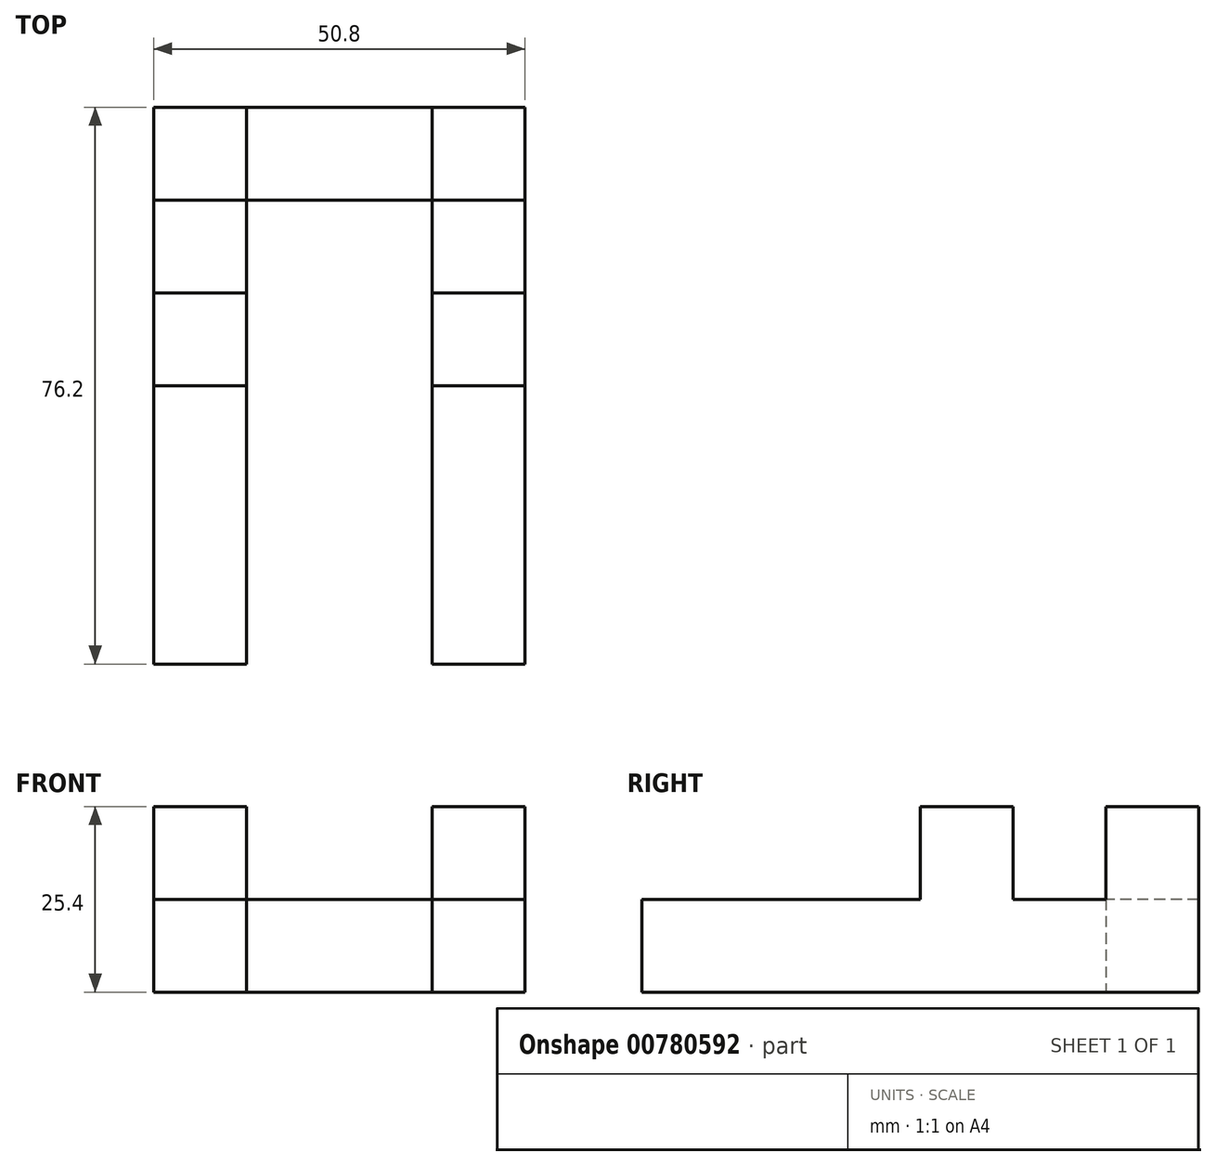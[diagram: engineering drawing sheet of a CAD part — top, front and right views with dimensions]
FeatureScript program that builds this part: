
annotation { "Feature Type Name" : "Feature", "Feature Type Description" : "" }
export const myFeature = defineFeature(function(context is Context, id is Id, definition is map)
    precondition{}
    {
        {
            var Q0;
            Q0=qCreatedBy(makeId("Top.planeOp"),FACE);
            var sketch = newSketch(context, id + "F0", { "sketchPlane" : qUnion([Q0])});
            skLineSegment(sketch, "E0", {"start": v(-40.53, -40.85) * mm, "end": v(-40.53, 35.35) * mm});
            skLineSegment(sketch, "E1", {"start": v(-40.53, 35.35) * mm, "end": v(10.27, 35.35) * mm});
            skLineSegment(sketch, "E2", {"start": v(10.27, 35.35) * mm, "end": v(10.27, -40.85) * mm});
            skLineSegment(sketch, "E3", {"start": v(-40.53, -40.85) * mm, "end": v(-27.83, -40.85) * mm});
            skLineSegment(sketch, "E4", {"start": v(-27.83, -40.85) * mm, "end": v(-27.83, 22.65) * mm});
            skLineSegment(sketch, "E5", {"start": v(-27.83, 22.65) * mm, "end": v(-2.43, 22.65) * mm});
            skLineSegment(sketch, "E6", {"start": v(-2.43, 22.65) * mm, "end": v(-2.43, -40.85) * mm});
            skLineSegment(sketch, "E7.trimOffspring", {"start": v(-2.43, -40.85) * mm, "end": v(10.27, -40.85) * mm});
            skSolve(sketch);
        }
        {
            var Q0;
            Q0 = qSketchRegion(id + "F0", true);
            extrude(context, id + "F1", {"entities" : qUnion([Q0]), "depth" : 12.7 * mm, "offsetDistance" : 25.4 * mm});
        }
        {
            var Q0;
            Q0=makeQuery(id+"F1.opExtrude","CAP_FACE",FACE,{"disambiguationData":[OSD([sQuery(id+"F0.wireOp",EDGE,"E0"),sQuery(id+"F0.wireOp",EDGE,"E1"),sQuery(id+"F0.wireOp",EDGE,"E2"),sQuery(id+"F0.wireOp",EDGE,"E3"),sQuery(id+"F0.wireOp",EDGE,"E4"),sQuery(id+"F0.wireOp",EDGE,"E5"),sQuery(id+"F0.wireOp",EDGE,"E6"),sQuery(id+"F0.wireOp",EDGE,"E7.trimOffspring")])],"isStart":false});
            var sketch = newSketch(context, id + "F2", { "sketchPlane" : qUnion([Q0])});
            skLineSegment(sketch, "E8.bottom", {"start": v(-40.53, 35.35) * mm, "end": v(-27.83, 35.35) * mm});
            skLineSegment(sketch, "E8.top", {"start": v(-40.53, 22.65) * mm, "end": v(-27.83, 22.65) * mm});
            skLineSegment(sketch, "E8.left", {"start": v(-40.53, 35.35) * mm, "end": v(-40.53, 22.65) * mm});
            skLineSegment(sketch, "E8.right", {"start": v(-27.83, 35.35) * mm, "end": v(-27.83, 22.65) * mm});
            skLineSegment(sketch, "E9.bottom", {"start": v(10.27, 35.35) * mm, "end": v(-2.43, 35.35) * mm});
            skLineSegment(sketch, "E9.top", {"start": v(10.27, 22.65) * mm, "end": v(-2.43, 22.65) * mm});
            skLineSegment(sketch, "E9.left", {"start": v(10.27, 35.35) * mm, "end": v(10.27, 22.65) * mm});
            skLineSegment(sketch, "E9.right", {"start": v(-2.43, 35.35) * mm, "end": v(-2.43, 22.65) * mm});
            skLineSegment(sketch, "E10", {"start": v(-27.83, 22.65) * mm, "end": v(-27.83, 9.95) * mm});
            skLineSegment(sketch, "E11", {"start": v(-27.83, 9.95) * mm, "end": v(-40.53, 9.95) * mm});
            skLineSegment(sketch, "E12", {"start": v(-40.53, 9.95) * mm, "end": v(-40.53, -2.75) * mm});
            skLineSegment(sketch, "E13", {"start": v(-40.53, -2.75) * mm, "end": v(-27.83, -2.75) * mm});
            skLineSegment(sketch, "E14", {"start": v(-27.83, -2.75) * mm, "end": v(-27.83, 9.95) * mm});
            skLineSegment(sketch, "E15", {"start": v(-2.43, 9.95) * mm, "end": v(10.27, 9.95) * mm});
            skLineSegment(sketch, "E16", {"start": v(-2.43, -2.75) * mm, "end": v(10.27, -2.75) * mm});
            skLineSegment(sketch, "E17", {"start": v(10.27, 9.95) * mm, "end": v(10.27, -2.75) * mm});
            skLineSegment(sketch, "E18", {"start": v(-2.43, 9.95) * mm, "end": v(-2.43, -2.75) * mm});
            skSolve(sketch);
        }
        {
            var Q0;
            Q0 = qSketchRegion(id + "F2", true);
            extrude(context, id + "F3", {"entities" : qUnion([Q0]), "operationType" : NewBodyOperationType.ADD, "depth" : 12.7 * mm, "offsetDistance" : 25.4 * mm});
        }
    });
